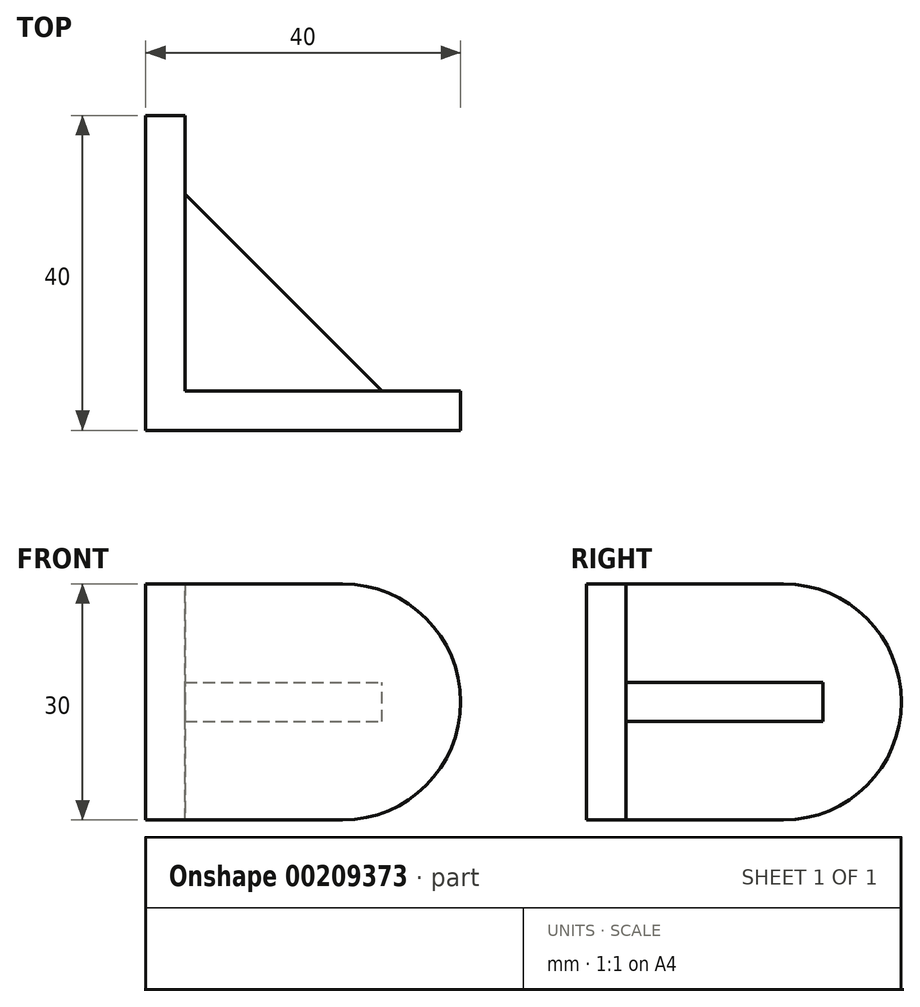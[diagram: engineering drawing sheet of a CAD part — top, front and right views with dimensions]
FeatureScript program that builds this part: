
annotation { "Feature Type Name" : "Feature", "Feature Type Description" : "" }
export const myFeature = defineFeature(function(context is Context, id is Id, definition is map)
    precondition{}
    {
        {
            var Q0;
            Q0=qCreatedBy(makeId("Top.planeOp"),FACE);
            var sketch = newSketch(context, id + "F0", { "sketchPlane" : qUnion([Q0])});
            skLineSegment(sketch, "E0", {"start": v(0, 0) * mm, "end": v(0, 40) * mm});
            skLineSegment(sketch, "E1", {"start": v(0, 40) * mm, "end": v(5, 40) * mm});
            skLineSegment(sketch, "E2", {"start": v(5, 40) * mm, "end": v(5, 5) * mm});
            skLineSegment(sketch, "E3", {"start": v(5, 5) * mm, "end": v(40, 5) * mm});
            skLineSegment(sketch, "E4", {"start": v(40, 5) * mm, "end": v(40, 0) * mm});
            skLineSegment(sketch, "E5", {"start": v(40, 0) * mm, "end": v(0, 0) * mm});
            skSolve(sketch);
        }
        {
            var Q0;
            Q0=makeQuery(id+"F0.imprint","IMPRINT",FACE,{"disambiguationData":[TD([[makeQuery(id+"F0.imprint","IMPRINT",EDGE,{"derivedFrom":sQuery(id+"F0.wireOp",EDGE,"E0")}),-1.0]])]});
            extrude(context, id + "F1", {"entities" : qUnion([Q0]), "depth" : 30 * mm});
        }
        {
            var Q0;
            Q0=makeQuery(id+"F1.opExtrude","SWEPT_FACE",FACE,{"disambiguationData":[OSD([sQuery(id+"F0.wireOp",EDGE,"E2")])]});
            var sketch = newSketch(context, id + "F2", { "sketchPlane" : qUnion([Q0])});
            skLineSegment(sketch, "E6.bottom", {"start": v(5, 30) * mm, "end": v(25, 30) * mm});
            skLineSegment(sketch, "E6.top", {"start": v(5, 0) * mm, "end": v(25, 0) * mm});
            skLineSegment(sketch, "E6.left", {"start": v(5, 30) * mm, "end": v(5, 0) * mm});
            skArc(sketch, "E7", {"start": v(25, 0) * mm, "mid": v(40, 15) * mm, "end": v(25, 30) * mm});
            skSolve(sketch);
        }
        {
            var Q0;
            {var subQ0=sQuery(id+"F2.wireOp",EDGE,"E7");var subQ1=sQuery(id+"F0.wireOp",EDGE,"E2");var subQ2=makeQuery(id+"F1.opExtrude","CAP_EDGE",EDGE,{"disambiguationData":[OSD([subQ1])],"isStart":false});var subQ3=makeQuery(id+"F2.imprint","INTERSECT",VERTEX,{"derivedFrom":[subQ2,sQuery(id+"F2.wireOp",EDGE,"E6.bottom"),subQ0]});Q0=makeQuery(id+"F2.imprint","IMPRINT",FACE,{"disambiguationData":[TD([[makeQuery(id+"F2.imprint","IMPRINT",EDGE,{"disambiguationData":[TD([[subQ3,1.0]])],"derivedFrom":subQ0}),-1.0]])]});}
            var Q1;
            {var subQ0=sQuery(id+"F2.wireOp",EDGE,"E7");var subQ1=sQuery(id+"F0.wireOp",EDGE,"E2");var subQ2=makeQuery(id+"F1.opExtrude","CAP_EDGE",EDGE,{"disambiguationData":[OSD([subQ1])],"isStart":true});var subQ3=makeQuery(id+"F2.imprint","INTERSECT",VERTEX,{"derivedFrom":[subQ2,sQuery(id+"F2.wireOp",EDGE,"E6.top"),subQ0]});Q1=makeQuery(id+"F2.imprint","IMPRINT",FACE,{"disambiguationData":[TD([[makeQuery(id+"F2.imprint","IMPRINT",EDGE,{"disambiguationData":[TD([[subQ3,-1.0]])],"derivedFrom":subQ0}),-1.0]])]});}
            extrude(context, id + "F3", {"entities" : qUnion([Q0, Q1]), "operationType" : NewBodyOperationType.REMOVE, "oppositeDirection" : true, "depth" : 25 * mm});
        }
        {
            var Q0;
            Q0=makeQuery(id+"F1.opExtrude","SWEPT_FACE",FACE,{"disambiguationData":[OSD([sQuery(id+"F0.wireOp",EDGE,"E3")])]});
            var sketch = newSketch(context, id + "F4", { "sketchPlane" : qUnion([Q0])});
            skLineSegment(sketch, "E8", {"start": v(-5, 30) * mm, "end": v(-5, 0) * mm});
            skLineSegment(sketch, "E9", {"start": v(-5, 0) * mm, "end": v(-25, 0) * mm});
            skLineSegment(sketch, "E10", {"start": v(-25, 30) * mm, "end": v(-5, 30) * mm});
            skArc(sketch, "E11", {"start": v(-25, 30) * mm, "mid": v(-40, 15) * mm, "end": v(-25, 0) * mm});
            skSolve(sketch);
        }
        {
            var Q0;
            {var subQ0=sQuery(id+"F4.wireOp",EDGE,"E11");var subQ1=sQuery(id+"F0.wireOp",EDGE,"E3");var subQ2=makeQuery(id+"F1.opExtrude","CAP_EDGE",EDGE,{"disambiguationData":[OSD([subQ1])],"isStart":false});var subQ3=makeQuery(id+"F4.imprint","INTERSECT",VERTEX,{"derivedFrom":[subQ2,sQuery(id+"F4.wireOp",EDGE,"E10"),subQ0]});Q0=makeQuery(id+"F4.imprint","IMPRINT",FACE,{"disambiguationData":[TD([[makeQuery(id+"F4.imprint","IMPRINT",EDGE,{"disambiguationData":[TD([[subQ3,-1.0]])],"derivedFrom":subQ0}),-1.0]])]});}
            var Q1;
            {var subQ0=sQuery(id+"F4.wireOp",EDGE,"E11");var subQ1=sQuery(id+"F0.wireOp",EDGE,"E3");var subQ2=makeQuery(id+"F1.opExtrude","CAP_EDGE",EDGE,{"disambiguationData":[OSD([subQ1])],"isStart":true});var subQ3=makeQuery(id+"F4.imprint","INTERSECT",VERTEX,{"derivedFrom":[subQ2,sQuery(id+"F4.wireOp",EDGE,"E9"),subQ0]});Q1=makeQuery(id+"F4.imprint","IMPRINT",FACE,{"disambiguationData":[TD([[makeQuery(id+"F4.imprint","IMPRINT",EDGE,{"disambiguationData":[TD([[subQ3,1.0]])],"derivedFrom":subQ0}),-1.0]])]});}
            extrude(context, id + "F5", {"entities" : qUnion([Q0, Q1]), "operationType" : NewBodyOperationType.REMOVE, "oppositeDirection" : true, "depth" : 25 * mm});
        }
        {
            var Q0;
            Q0=makeQuery(id+"F1.opExtrude","CAP_FACE",FACE,{"disambiguationData":[OSD([sQuery(id+"F0.wireOp",EDGE,"E0"),sQuery(id+"F0.wireOp",EDGE,"E1"),sQuery(id+"F0.wireOp",EDGE,"E2"),sQuery(id+"F0.wireOp",EDGE,"E3"),sQuery(id+"F0.wireOp",EDGE,"E4"),sQuery(id+"F0.wireOp",EDGE,"E5")])],"isStart":false});
            var sketch = newSketch(context, id + "F6", { "sketchPlane" : qUnion([Q0])});
            skLineSegment(sketch, "E12", {"start": v(5, 5) * mm, "end": v(30, 5) * mm});
            skLineSegment(sketch, "E13", {"start": v(5, 5) * mm, "end": v(5, 30) * mm});
            skLineSegment(sketch, "E14", {"start": v(5, 30) * mm, "end": v(30, 5) * mm});
            skSolve(sketch);
        }
        {
            var Q0;
            {var subQ2=sQuery(id+"F6.wireOp",EDGE,"E14");Q0=makeQuery(id+"F6.imprint","IMPRINT",FACE,{"disambiguationData":[TD([[makeQuery(id+"F6.imprint","IMPRINT",EDGE,{"derivedFrom":subQ2}),-1.0]])]});}
            extrude(context, id + "F7", {"entities" : qUnion([Q0]), "oppositeDirection" : true, "depth" : 17.5 * mm});
        }
        {
            var Q0;
            Q0=makeQuery(id+"F7.opExtrude","CAP_FACE",FACE,{"disambiguationData":[OSD([sQuery(id+"F6.wireOp",EDGE,"E12"),sQuery(id+"F6.wireOp",EDGE,"E13"),sQuery(id+"F6.wireOp",EDGE,"E14")])],"isStart":true});
            extrude(context, id + "F8", {"entities" : qUnion([Q0]), "operationType" : NewBodyOperationType.REMOVE, "oppositeDirection" : true, "depth" : 12.5 * mm});
        }
    });
